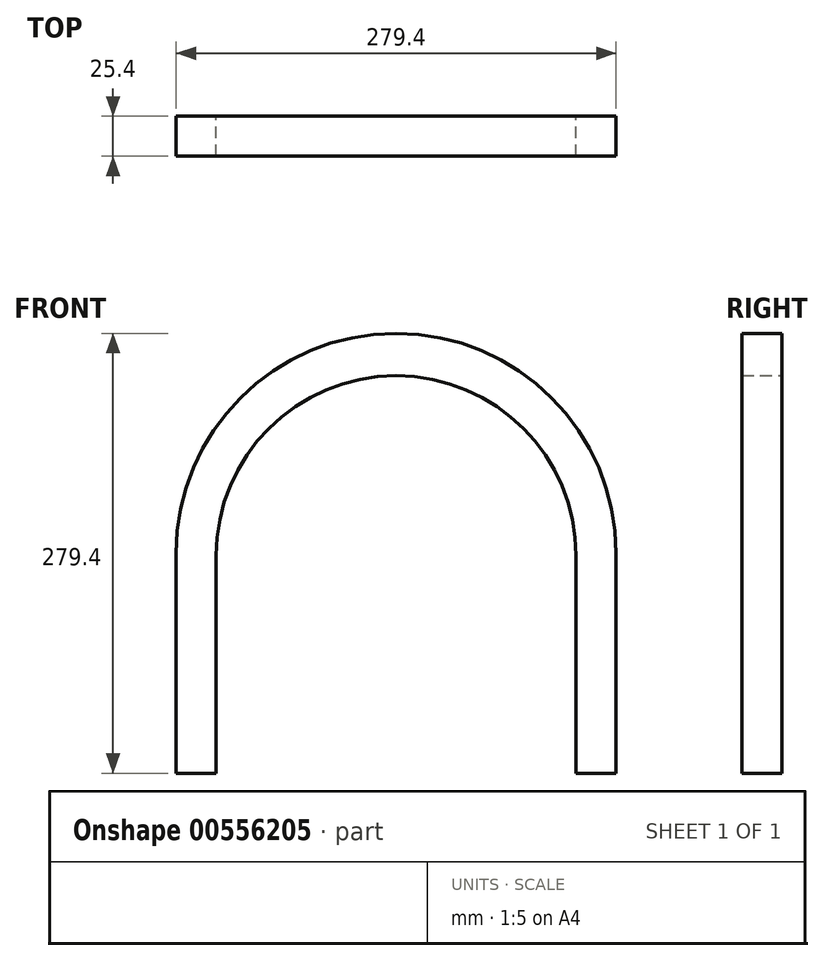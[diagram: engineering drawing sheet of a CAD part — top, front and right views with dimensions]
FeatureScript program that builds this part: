
annotation { "Feature Type Name" : "Feature", "Feature Type Description" : "" }
export const myFeature = defineFeature(function(context is Context, id is Id, definition is map)
    precondition{}
    {
        {
            var Q0;
            Q0=qCreatedBy(makeId("Front.planeOp"),FACE);
            var sketch = newSketch(context, id + "F0", { "sketchPlane" : qUnion([Q0])});
            skArc(sketch, "E0", {"start": v(139.7, 0) * mm, "mid": v(0, 139.7) * mm, "end": v(-139.7, 0) * mm});
            skArc(sketch, "E1", {"start": v(114.3, -1.5) * mm, "mid": v(0, 112.8) * mm, "end": v(-114.3, -1.5) * mm});
            skLineSegment(sketch, "E2", {"start": v(-139.7, 0) * mm, "end": v(-139.7, -139.7) * mm});
            skLineSegment(sketch, "E3", {"start": v(-139.7, -139.7) * mm, "end": v(-114.3, -139.7) * mm});
            skLineSegment(sketch, "E4", {"start": v(-114.3, -139.7) * mm, "end": v(-114.3, 0) * mm});
            skLineSegment(sketch, "E5", {"start": v(139.7, 0) * mm, "end": v(139.7, -139.7) * mm});
            skLineSegment(sketch, "E6", {"start": v(139.7, -139.7) * mm, "end": v(114.3, -139.7) * mm});
            skLineSegment(sketch, "E7", {"start": v(114.3, -139.7) * mm, "end": v(114.3, 0) * mm});
            skSolve(sketch);
        }
        {
            var Q0;
            Q0 = qSketchRegion(id + "F0", true);
            extrude(context, id + "F1", {"entities" : qUnion([Q0]), "depth" : 25.4 * mm, "offsetDistance" : 25.4 * mm});
        }
    });
